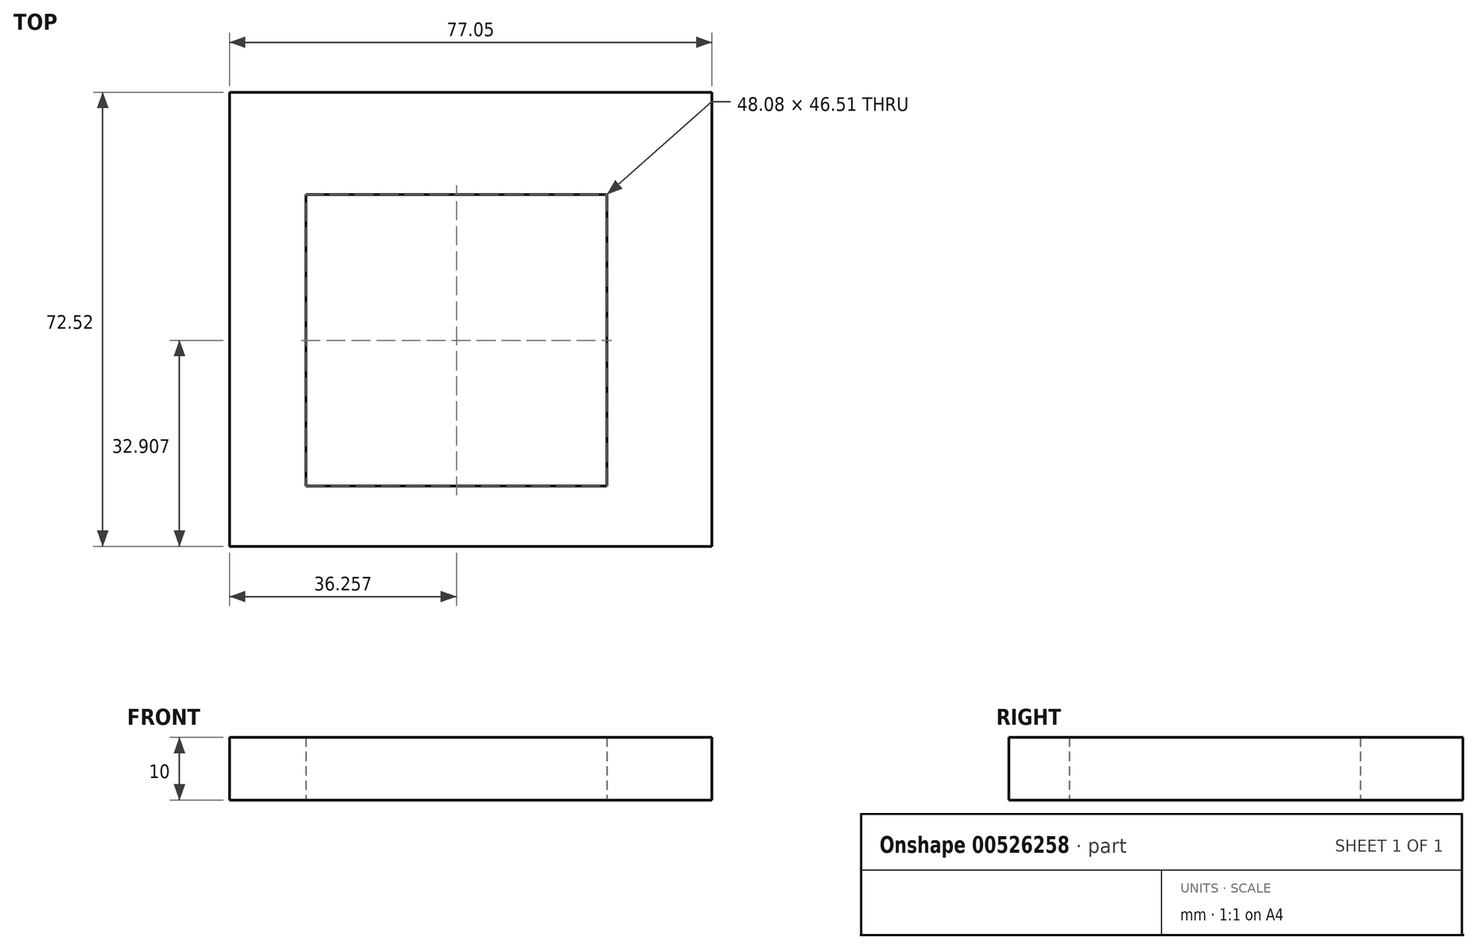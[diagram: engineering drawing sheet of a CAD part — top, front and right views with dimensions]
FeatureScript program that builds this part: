
annotation { "Feature Type Name" : "Feature", "Feature Type Description" : "" }
export const myFeature = defineFeature(function(context is Context, id is Id, definition is map)
    precondition{}
    {
        {
            var Q0;
            Q0=qCreatedBy(makeId("Top.planeOp"),FACE);
            var sketch = newSketch(context, id + "F0", { "sketchPlane" : qUnion([Q0])});
            skLineSegment(sketch, "E0.bottom", {"start": v(-29.36, -29.36) * mm, "end": v(47.7, -29.36) * mm});
            skLineSegment(sketch, "E0.top", {"start": v(-29.36, 43.16) * mm, "end": v(47.7, 43.16) * mm});
            skLineSegment(sketch, "E0.left", {"start": v(-29.36, -29.36) * mm, "end": v(-29.36, 43.16) * mm});
            skLineSegment(sketch, "E0.right", {"start": v(47.7, -29.36) * mm, "end": v(47.7, 43.16) * mm});
            skLineSegment(sketch, "E1.bottom", {"start": v(-17.15, -19.7) * mm, "end": v(30.94, -19.7) * mm});
            skLineSegment(sketch, "E1.top", {"start": v(-17.15, 26.8) * mm, "end": v(30.94, 26.8) * mm});
            skLineSegment(sketch, "E1.left", {"start": v(-17.15, -19.7) * mm, "end": v(-17.15, 26.8) * mm});
            skLineSegment(sketch, "E1.right", {"start": v(30.94, -19.7) * mm, "end": v(30.94, 26.8) * mm});
            skSolve(sketch);
        }
        {
            var Q0;
            Q0=makeQuery(id+"F0.imprint","IMPRINT",FACE,{"disambiguationData":[TD([[makeQuery(id+"F0.imprint","IMPRINT",EDGE,{"derivedFrom":sQuery(id+"F0.wireOp",EDGE,"E0.bottom")}),1.0]])]});
            extrude(context, id + "F1", {"entities" : qUnion([Q0]), "depth" : 10 * mm, "offsetDistance" : 25.4 * mm});
        }
    });
